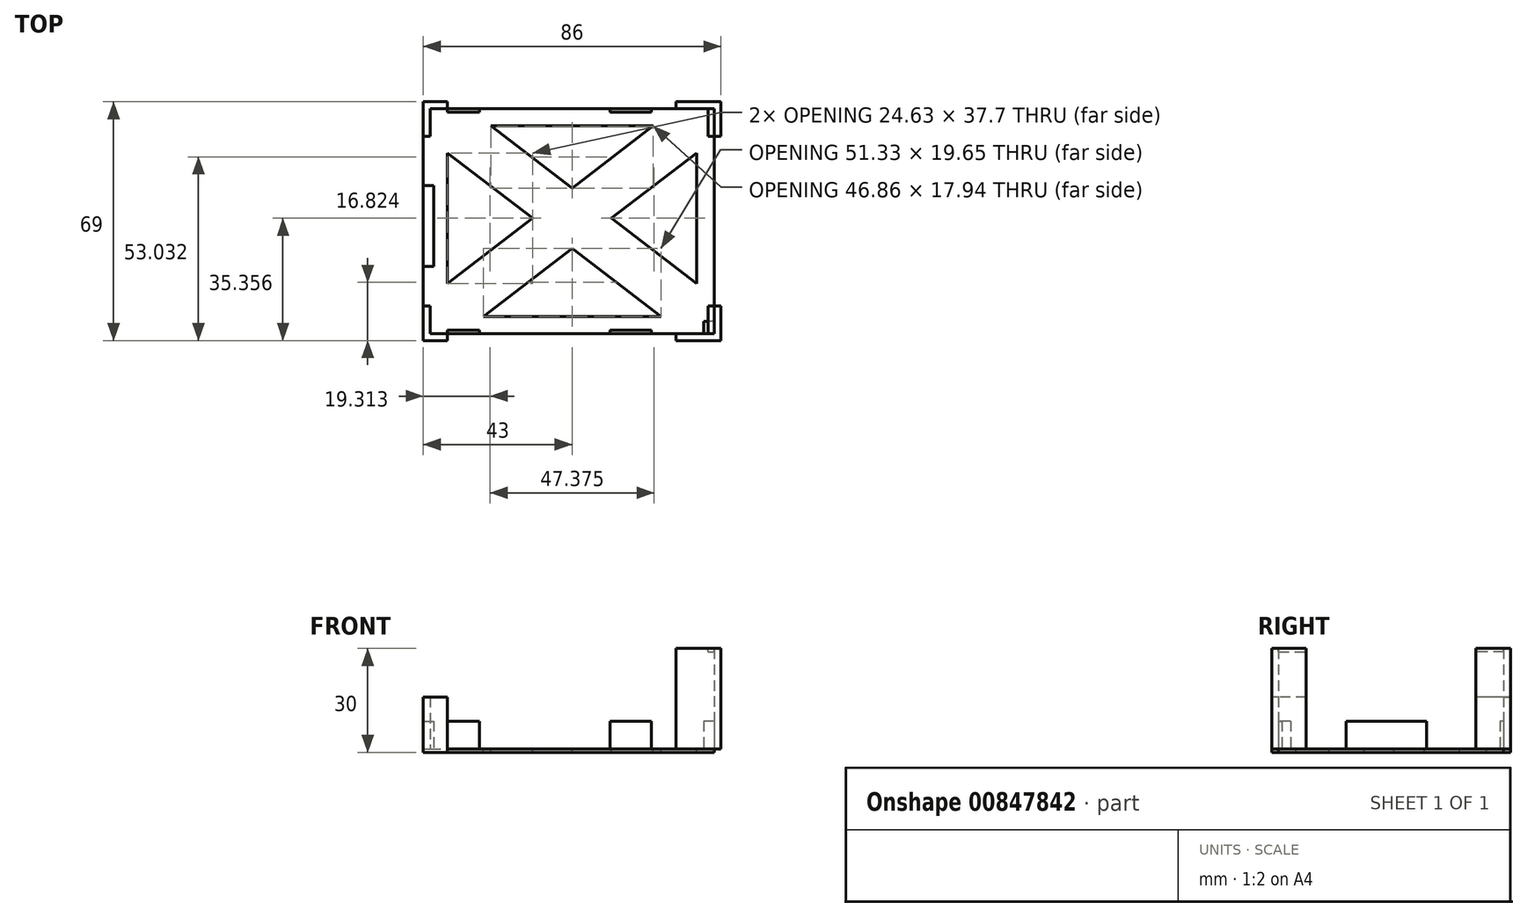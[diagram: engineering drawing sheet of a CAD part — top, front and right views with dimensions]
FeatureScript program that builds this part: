
annotation { "Feature Type Name" : "Feature", "Feature Type Description" : "" }
export const myFeature = defineFeature(function(context is Context, id is Id, definition is map)
    precondition{}
    {
        {
            var Q0;
            Q0=qCreatedBy(makeId("Top.planeOp"),FACE);
            var sketch = newSketch(context, id + "F0", { "sketchPlane" : qUnion([Q0])});
            skLineSegment(sketch, "E0", {"start": v(0, 51.21) * mm, "end": v(0, -60.35) * mm, "construction": true});
            skLineSegment(sketch, "E1", {"start": v(-52.5, 0) * mm, "end": v(66.1, 0) * mm, "construction": true});
            skLineSegment(sketch, "E2.bottom", {"start": v(-41, 32.5) * mm, "end": v(41, 32.5) * mm});
            skLineSegment(sketch, "E2.top", {"start": v(-41, -32.5) * mm, "end": v(41, -32.5) * mm});
            skLineSegment(sketch, "E2.left", {"start": v(-41, 32.5) * mm, "end": v(-41, -32.5) * mm});
            skLineSegment(sketch, "E2.right", {"start": v(41, 32.5) * mm, "end": v(41, -32.5) * mm});
            skPoint(sketch, "E3", {"position": v(0, 32.5) * mm});
            skPoint(sketch, "E4", {"position": v(41, 0) * mm});
            skSolve(sketch);
        }
        {
            var Q0;
            Q0 = qSketchRegion(id + "F0", true);
            extrude(context, id + "F1", {"entities" : qUnion([Q0]), "depth" : 1 * mm, "offsetDistance" : 25 * mm});
        }
        {
            var Q0;
            Q0=makeQuery(id+"F1.opExtrude","CAP_FACE",FACE,{"disambiguationData":[OSD([sQuery(id+"F0.wireOp",EDGE,"E2.bottom"),sQuery(id+"F0.wireOp",EDGE,"E2.top"),sQuery(id+"F0.wireOp",EDGE,"E2.left"),sQuery(id+"F0.wireOp",EDGE,"E2.right")])],"isStart":false});
            var sketch = newSketch(context, id + "F2", { "sketchPlane" : qUnion([Q0])});
            skLineSegment(sketch, "E5.bottom", {"start": v(-41, 32.5) * mm, "end": v(-43, 32.5) * mm});
            skLineSegment(sketch, "E5.top", {"start": v(-41, -32.5) * mm, "end": v(-43, -32.5) * mm});
            skLineSegment(sketch, "E5.left", {"start": v(-41, 32.5) * mm, "end": v(-41, -32.5) * mm});
            skLineSegment(sketch, "E5.right", {"start": v(-43, 32.5) * mm, "end": v(-43, -32.5) * mm});
            skLineSegment(sketch, "E6.bottom", {"start": v(41, 32.5) * mm, "end": v(43, 32.5) * mm});
            skLineSegment(sketch, "E6.top", {"start": v(41, -32.5) * mm, "end": v(43, -32.5) * mm});
            skLineSegment(sketch, "E6.left", {"start": v(41, 32.5) * mm, "end": v(41, -32.5) * mm});
            skLineSegment(sketch, "E6.right", {"start": v(43, 32.5) * mm, "end": v(43, -32.5) * mm});
            skLineSegment(sketch, "E7.bottom", {"start": v(30, 32.5) * mm, "end": v(43, 32.5) * mm});
            skLineSegment(sketch, "E7.top", {"start": v(30, 34.5) * mm, "end": v(43, 34.5) * mm});
            skLineSegment(sketch, "E7.left", {"start": v(30, 32.5) * mm, "end": v(30, 34.5) * mm});
            skLineSegment(sketch, "E7.right", {"start": v(43, 32.5) * mm, "end": v(43, 34.5) * mm});
            skLineSegment(sketch, "E8.bottom", {"start": v(30, -32.5) * mm, "end": v(43, -32.5) * mm});
            skLineSegment(sketch, "E8.top", {"start": v(30, -34.5) * mm, "end": v(43, -34.5) * mm});
            skLineSegment(sketch, "E8.left", {"start": v(30, -32.5) * mm, "end": v(30, -34.5) * mm});
            skLineSegment(sketch, "E8.right", {"start": v(43, -32.5) * mm, "end": v(43, -34.5) * mm});
            skLineSegment(sketch, "E9.bottom", {"start": v(-43, 32.5) * mm, "end": v(-36, 32.5) * mm});
            skLineSegment(sketch, "E9.top", {"start": v(-43, 34.5) * mm, "end": v(-36, 34.5) * mm});
            skLineSegment(sketch, "E9.left", {"start": v(-43, 32.5) * mm, "end": v(-43, 34.5) * mm});
            skLineSegment(sketch, "E9.right", {"start": v(-36, 32.5) * mm, "end": v(-36, 34.5) * mm});
            skLineSegment(sketch, "E10.bottom", {"start": v(-43, -32.5) * mm, "end": v(-36, -32.5) * mm});
            skLineSegment(sketch, "E10.top", {"start": v(-43, -34.5) * mm, "end": v(-36, -34.5) * mm});
            skLineSegment(sketch, "E10.left", {"start": v(-43, -32.5) * mm, "end": v(-43, -34.5) * mm});
            skLineSegment(sketch, "E10.right", {"start": v(-36, -32.5) * mm, "end": v(-36, -34.5) * mm});
            skSolve(sketch);
        }
        {
            var Q0;
            {var subQ9=sQuery(id+"F2.wireOp",EDGE,"E5.left");Q0=makeQuery(id+"F2.imprint","IMPRINT",FACE,{"disambiguationData":[TD([[makeQuery(id+"F2.imprint","IMPRINT",EDGE,{"derivedFrom":subQ9}),1.0]])]});}
            var sketch = newSketch(context, id + "F3", { "sketchPlane" : qUnion([Q0])});
            skLineSegment(sketch, "E11.bottom", {"start": v(-36, 27.5) * mm, "end": v(36, 27.5) * mm});
            skLineSegment(sketch, "E11.top", {"start": v(-36, -27.5) * mm, "end": v(36, -27.5) * mm});
            skLineSegment(sketch, "E11.left", {"start": v(-36, 27.5) * mm, "end": v(-36, -27.5) * mm});
            skLineSegment(sketch, "E11.right", {"start": v(36, 27.5) * mm, "end": v(36, -27.5) * mm});
            skLineSegment(sketch, "E12", {"start": v(23.43, 27.5) * mm, "end": v(-36, -18) * mm});
            skLineSegment(sketch, "E13", {"start": v(-36, -27.5) * mm, "end": v(36, 27.5) * mm, "construction": true});
            skLineSegment(sketch, "E14", {"start": v(-25.66, -27.5) * mm, "end": v(36, 19.7) * mm});
            skLineSegment(sketch, "E15", {"start": v(0, 35.79) * mm, "end": v(0, -35.94) * mm, "construction": true});
            skLineSegment(sketch, "E16.MirrorCS", {"start": v(-23.43, 27.5) * mm, "end": v(36, -18) * mm});
            skLineSegment(sketch, "E17.MirrorCS", {"start": v(25.66, -27.5) * mm, "end": v(-36, 19.7) * mm});
            skSolve(sketch);
        }
        {
            var Q0;
            {var subQ0=sQuery(id+"F3.wireOp",EDGE,"E12");var subQ1=sQuery(id+"F3.wireOp",EDGE,"E11.left");var subQ2=makeQuery(id+"F3.imprint","INTERSECT",VERTEX,{"derivedFrom":[subQ1,subQ0]});Q0=makeQuery(id+"F3.imprint","IMPRINT",FACE,{"disambiguationData":[TD([[makeQuery(id+"F3.imprint","IMPRINT",EDGE,{"disambiguationData":[TD([[subQ2,1.0]])],"derivedFrom":subQ1}),1.0]])]});}
            var Q1;
            {var subQ0=sQuery(id+"F3.wireOp",EDGE,"E12");var subQ1=sQuery(id+"F3.wireOp",EDGE,"E11.bottom");var subQ2=makeQuery(id+"F3.imprint","INTERSECT",VERTEX,{"derivedFrom":[subQ1,subQ0]});Q1=makeQuery(id+"F3.imprint","IMPRINT",FACE,{"disambiguationData":[TD([[makeQuery(id+"F3.imprint","IMPRINT",EDGE,{"disambiguationData":[TD([[subQ2,1.0]])],"derivedFrom":subQ1}),-1.0]])]});}
            var Q2;
            {var subQ0=sQuery(id+"F3.wireOp",EDGE,"E14");var subQ1=sQuery(id+"F3.wireOp",EDGE,"E11.right");var subQ2=makeQuery(id+"F3.imprint","INTERSECT",VERTEX,{"derivedFrom":[subQ1,subQ0]});Q2=makeQuery(id+"F3.imprint","IMPRINT",FACE,{"disambiguationData":[TD([[makeQuery(id+"F3.imprint","IMPRINT",EDGE,{"disambiguationData":[TD([[subQ2,-1.0]])],"derivedFrom":subQ1}),-1.0]])]});}
            var Q3;
            {var subQ0=sQuery(id+"F3.wireOp",EDGE,"E14");var subQ1=sQuery(id+"F3.wireOp",EDGE,"E11.top");var subQ2=makeQuery(id+"F3.imprint","INTERSECT",VERTEX,{"derivedFrom":[subQ1,subQ0]});Q3=makeQuery(id+"F3.imprint","IMPRINT",FACE,{"disambiguationData":[TD([[makeQuery(id+"F3.imprint","IMPRINT",EDGE,{"disambiguationData":[TD([[subQ2,-1.0]])],"derivedFrom":subQ1}),1.0]])]});}
            extrude(context, id + "F4", {"entities" : qUnion([Q0, Q1, Q2, Q3]), "operationType" : NewBodyOperationType.REMOVE, "oppositeDirection" : true, "depth" : 100 * mm, "offsetDistance" : 25 * mm});
        }
        {
            var Q0;
            {var subQ0=sQuery(id+"F2.wireOp",EDGE,"E5.left");Q0=makeQuery(id+"F2.imprint","IMPRINT",FACE,{"disambiguationData":[TD([[makeQuery(id+"F2.imprint","IMPRINT",EDGE,{"derivedFrom":subQ0}),-1.0]])]});}
            var Q1;
            Q1=makeQuery(id+"F2.imprint","IMPRINT",FACE,{"disambiguationData":[TD([[makeQuery(id+"F2.imprint","IMPRINT",EDGE,{"derivedFrom":sQuery(id+"F2.wireOp",EDGE,"E9.top")}),-1.0]])]});
            var Q2;
            Q2=makeQuery(id+"F2.imprint","IMPRINT",FACE,{"disambiguationData":[TD([[makeQuery(id+"F2.imprint","IMPRINT",EDGE,{"derivedFrom":sQuery(id+"F2.wireOp",EDGE,"E10.top")}),1.0]])]});
            var Q3;
            {var subQ0=sQuery(id+"F3.wireOp",EDGE,"E12");var subQ1=sQuery(id+"F3.wireOp",EDGE,"E11.left");Q3=makeQuery(id+"F4.boolean.opBoolean","INTERSECT",VERTEX,{"derivedFrom":[makeQuery(id+"F1.opExtrude","CAP_FACE",FACE,{"disambiguationData":[OSD([sQuery(id+"F0.wireOp",EDGE,"E2.bottom"),sQuery(id+"F0.wireOp",EDGE,"E2.top"),sQuery(id+"F0.wireOp",EDGE,"E2.left"),sQuery(id+"F0.wireOp",EDGE,"E2.right")])],"isStart":true}),makeQuery(id+"F4.opExtrude","SWEPT_FACE",FACE,{"disambiguationData":[OSD([subQ1])]}),makeQuery(id+"F4.opExtrude","SWEPT_FACE",FACE,{"disambiguationData":[OSD([subQ0]),TDD([makeQuery(id+"F3.imprint","IMPRINT",EDGE,{"disambiguationData":[TD([[makeQuery(id+"F3.imprint","INTERSECT",VERTEX,{"derivedFrom":[subQ1,subQ0]}),1.0]])],"derivedFrom":subQ0})])]})]});}
            extrude(context, id + "F5", {"entities" : qUnion([Q0, Q1, Q2]), "operationType" : NewBodyOperationType.ADD, "depth" : 15 * mm, "offsetDistance" : 25 * mm, "hasSecondDirection" : true, "secondDirectionBound" : SecondDirectionBoundingType.UP_TO_VERTEX, "secondDirectionOppositeDirection" : true, "secondDirectionDepth" : 1 * mm, "secondDirectionBoundEntityVertex" : qUnion([Q3])});
        }
        {
            var Q0;
            Q0=makeQuery(id+"F2.imprint","IMPRINT",FACE,{"disambiguationData":[TD([[makeQuery(id+"F2.imprint","IMPRINT",EDGE,{"derivedFrom":sQuery(id+"F2.wireOp",EDGE,"E7.top")}),-1.0]])]});
            var Q1;
            {var subQ0=sQuery(id+"F2.wireOp",EDGE,"E6.left");Q1=makeQuery(id+"F2.imprint","IMPRINT",FACE,{"disambiguationData":[TD([[makeQuery(id+"F2.imprint","IMPRINT",EDGE,{"derivedFrom":subQ0}),1.0]])]});}
            var Q2;
            Q2=makeQuery(id+"F2.imprint","IMPRINT",FACE,{"disambiguationData":[TD([[makeQuery(id+"F2.imprint","IMPRINT",EDGE,{"derivedFrom":sQuery(id+"F2.wireOp",EDGE,"E8.top")}),1.0]])]});
            extrude(context, id + "F6", {"entities" : qUnion([Q0, Q1, Q2]), "depth" : 29 * mm, "offsetDistance" : 25 * mm});
        }
        {
            var Q0;
            Q0=makeQuery(id+"F6.opExtrude","SWEPT_FACE",FACE,{"disambiguationData":[OSD([sQuery(id+"F2.wireOp",EDGE,"E6.right"),sQuery(id+"F2.wireOp",EDGE,"E7.right"),sQuery(id+"F2.wireOp",EDGE,"E8.right")])]});
            var sketch = newSketch(context, id + "F7", { "sketchPlane" : qUnion([Q0])});
            skLineSegment(sketch, "E18.bottom", {"start": v(-24.5, 30) * mm, "end": v(24.5, 30) * mm});
            skLineSegment(sketch, "E18.top", {"start": v(-24.5, 1) * mm, "end": v(24.5, 1) * mm});
            skLineSegment(sketch, "E18.left", {"start": v(-24.5, 30) * mm, "end": v(-24.5, 1) * mm});
            skLineSegment(sketch, "E18.right", {"start": v(24.5, 30) * mm, "end": v(24.5, 1) * mm});
            skSolve(sketch);
        }
        {
            var Q0;
            Q0 = qSketchRegion(id + "F7", true);
            var Q1;
            Q1=makeQuery(id+"F5.opExtrude","CAP_VERTEX",VERTEX,{"disambiguationData":[OSD([sQuery(id+"F2.wireOp",EDGE,"E9.top"),sQuery(id+"F2.wireOp",EDGE,"E9.left")])],"isStart":false});
            extrude(context, id + "F8", {"entities" : qUnion([Q0]), "operationType" : NewBodyOperationType.REMOVE, "endBound" : BoundingType.THROUGH_ALL, "oppositeDirection" : true, "depth" : 100 * mm, "endBoundEntityVertex" : qUnion([Q1]), "offsetDistance" : 25 * mm});
        }
        {
            var Q0;
            Q0=makeQuery(id+"F8.boolean.opBoolean","MERGE",FACE,{"derivedFrom":[makeQuery(id+"F1.opExtrude","CAP_FACE",FACE,{"disambiguationData":[OSD([sQuery(id+"F0.wireOp",EDGE,"E2.bottom"),sQuery(id+"F0.wireOp",EDGE,"E2.top"),sQuery(id+"F0.wireOp",EDGE,"E2.left"),sQuery(id+"F0.wireOp",EDGE,"E2.right")])],"isStart":false})],"fromTools":[makeQuery(id+"F8.opExtrude","SWEPT_FACE",FACE,{"disambiguationData":[OSD([sQuery(id+"F7.wireOp",EDGE,"E18.top")])]})]});
            var sketch = newSketch(context, id + "F9", { "sketchPlane" : qUnion([Q0])});
            skLineSegment(sketch, "E19.bottom", {"start": v(-43, 10.26) * mm, "end": v(-40, 10.26) * mm});
            skLineSegment(sketch, "E19.top", {"start": v(-43, -13.03) * mm, "end": v(-40, -13.03) * mm});
            skLineSegment(sketch, "E19.left", {"start": v(-43, 10.26) * mm, "end": v(-43, -13.03) * mm});
            skLineSegment(sketch, "E19.right", {"start": v(-40, 10.26) * mm, "end": v(-40, -13.03) * mm});
            skLineSegment(sketch, "E20.bottom", {"start": v(-36, 32.5) * mm, "end": v(-26.79, 32.5) * mm});
            skLineSegment(sketch, "E20.top", {"start": v(-36, 31.5) * mm, "end": v(-26.79, 31.5) * mm});
            skLineSegment(sketch, "E20.left", {"start": v(-36, 32.5) * mm, "end": v(-36, 31.5) * mm});
            skLineSegment(sketch, "E20.right", {"start": v(-26.79, 32.5) * mm, "end": v(-26.79, 31.5) * mm});
            skLineSegment(sketch, "E21.bottom", {"start": v(10.93, 32.5) * mm, "end": v(22.9, 32.5) * mm});
            skLineSegment(sketch, "E21.top", {"start": v(10.93, 31.5) * mm, "end": v(22.9, 31.5) * mm});
            skLineSegment(sketch, "E21.left", {"start": v(10.93, 32.5) * mm, "end": v(10.93, 31.5) * mm});
            skLineSegment(sketch, "E21.right", {"start": v(22.9, 32.5) * mm, "end": v(22.9, 31.5) * mm});
            skLineSegment(sketch, "E22", {"start": v(-51.4, 0) * mm, "end": v(60.62, 0) * mm, "construction": true});
            skLineSegment(sketch, "E23.MirrorCS", {"start": v(-26.79, -32.5) * mm, "end": v(-26.79, -31.5) * mm});
            skLineSegment(sketch, "E24.MirrorCS", {"start": v(22.9, -32.5) * mm, "end": v(22.9, -31.5) * mm});
            skLineSegment(sketch, "E25.MirrorCS", {"start": v(-36, -32.5) * mm, "end": v(-36, -31.5) * mm});
            skLineSegment(sketch, "E26.MirrorCS", {"start": v(10.93, -32.5) * mm, "end": v(10.93, -31.5) * mm});
            skLineSegment(sketch, "E27.MirrorCS", {"start": v(-36, -31.5) * mm, "end": v(-26.79, -31.5) * mm});
            skLineSegment(sketch, "E28.MirrorCS", {"start": v(10.93, -32.5) * mm, "end": v(22.9, -32.5) * mm});
            skLineSegment(sketch, "E29.MirrorCS", {"start": v(10.93, -31.5) * mm, "end": v(22.9, -31.5) * mm});
            skLineSegment(sketch, "E30.MirrorCS", {"start": v(-36, -32.5) * mm, "end": v(-26.79, -32.5) * mm});
            skLineSegment(sketch, "E31.bottom", {"start": v(41, -32.5) * mm, "end": v(37.99, -32.5) * mm});
            skLineSegment(sketch, "E31.top", {"start": v(41, -29) * mm, "end": v(37.99, -29) * mm});
            skLineSegment(sketch, "E31.left", {"start": v(41, -32.5) * mm, "end": v(41, -29) * mm});
            skLineSegment(sketch, "E31.right", {"start": v(37.99, -32.5) * mm, "end": v(37.99, -29) * mm});
            skSolve(sketch);
        }
        {
            var Q0;
            Q0 = qSketchRegion(id + "F9", true);
            extrude(context, id + "F10", {"entities" : qUnion([Q0]), "depth" : 8 * mm, "offsetDistance" : 25 * mm});
        }
        {
            var Q0;
            {var subQ0=sQuery(id+"F2.wireOp",EDGE,"E7.bottom");var subQ1=sQuery(id+"F2.wireOp",EDGE,"E8.right");var subQ2=sQuery(id+"F2.wireOp",EDGE,"E7.right");var subQ3=sQuery(id+"F2.wireOp",EDGE,"E6.right");var subQ4=sQuery(id+"F2.wireOp",EDGE,"E7.top");var subQ5=sQuery(id+"F2.wireOp",EDGE,"E6.left");var subQ6=sQuery(id+"F2.wireOp",EDGE,"E7.left");Q0=makeQuery(id+"F8.boolean.opBoolean","SPLIT",FACE,{"disambiguationData":[TD([makeQuery(id+"F6.opExtrude","SWEPT_FACE",FACE,{"disambiguationData":[OSD([subQ0])]})])],"derivedFrom":makeQuery(id+"F6.opExtrude","CAP_FACE",FACE,{"disambiguationData":[OSD([subQ5,subQ3,subQ0,subQ4,subQ6,subQ2,sQuery(id+"F2.wireOp",EDGE,"E8.bottom"),sQuery(id+"F2.wireOp",EDGE,"E8.top"),sQuery(id+"F2.wireOp",EDGE,"E8.left"),subQ1])],"isStart":false})});}
            var sketch = newSketch(context, id + "F11", { "sketchPlane" : qUnion([Q0])});
            skLineSegment(sketch, "E32.bottom", {"start": v(39.23, 32.5) * mm, "end": v(41, 32.5) * mm});
            skLineSegment(sketch, "E32.top", {"start": v(39.23, 24.5) * mm, "end": v(41, 24.5) * mm});
            skLineSegment(sketch, "E32.left", {"start": v(39.23, 32.5) * mm, "end": v(39.23, 24.5) * mm});
            skLineSegment(sketch, "E32.right", {"start": v(41, 32.5) * mm, "end": v(41, 24.5) * mm});
            skLineSegment(sketch, "E33", {"start": v(-5.04, 0) * mm, "end": v(26.99, 0) * mm, "construction": true});
            skLineSegment(sketch, "E34.MirrorCS", {"start": v(39.23, -32.5) * mm, "end": v(41, -32.5) * mm});
            skLineSegment(sketch, "E35.MirrorCS", {"start": v(39.23, -32.5) * mm, "end": v(39.23, -24.5) * mm});
            skLineSegment(sketch, "E36.MirrorCS", {"start": v(41, -32.5) * mm, "end": v(41, -24.5) * mm});
            skLineSegment(sketch, "E37.MirrorCS", {"start": v(39.23, -24.5) * mm, "end": v(41, -24.5) * mm});
            skSolve(sketch);
        }
        {
            var Q0;
            Q0 = qSketchRegion(id + "F11", true);
            extrude(context, id + "F12", {"entities" : qUnion([Q0]), "oppositeDirection" : true, "depth" : 1 * mm, "offsetDistance" : 25 * mm});
        }
    });
